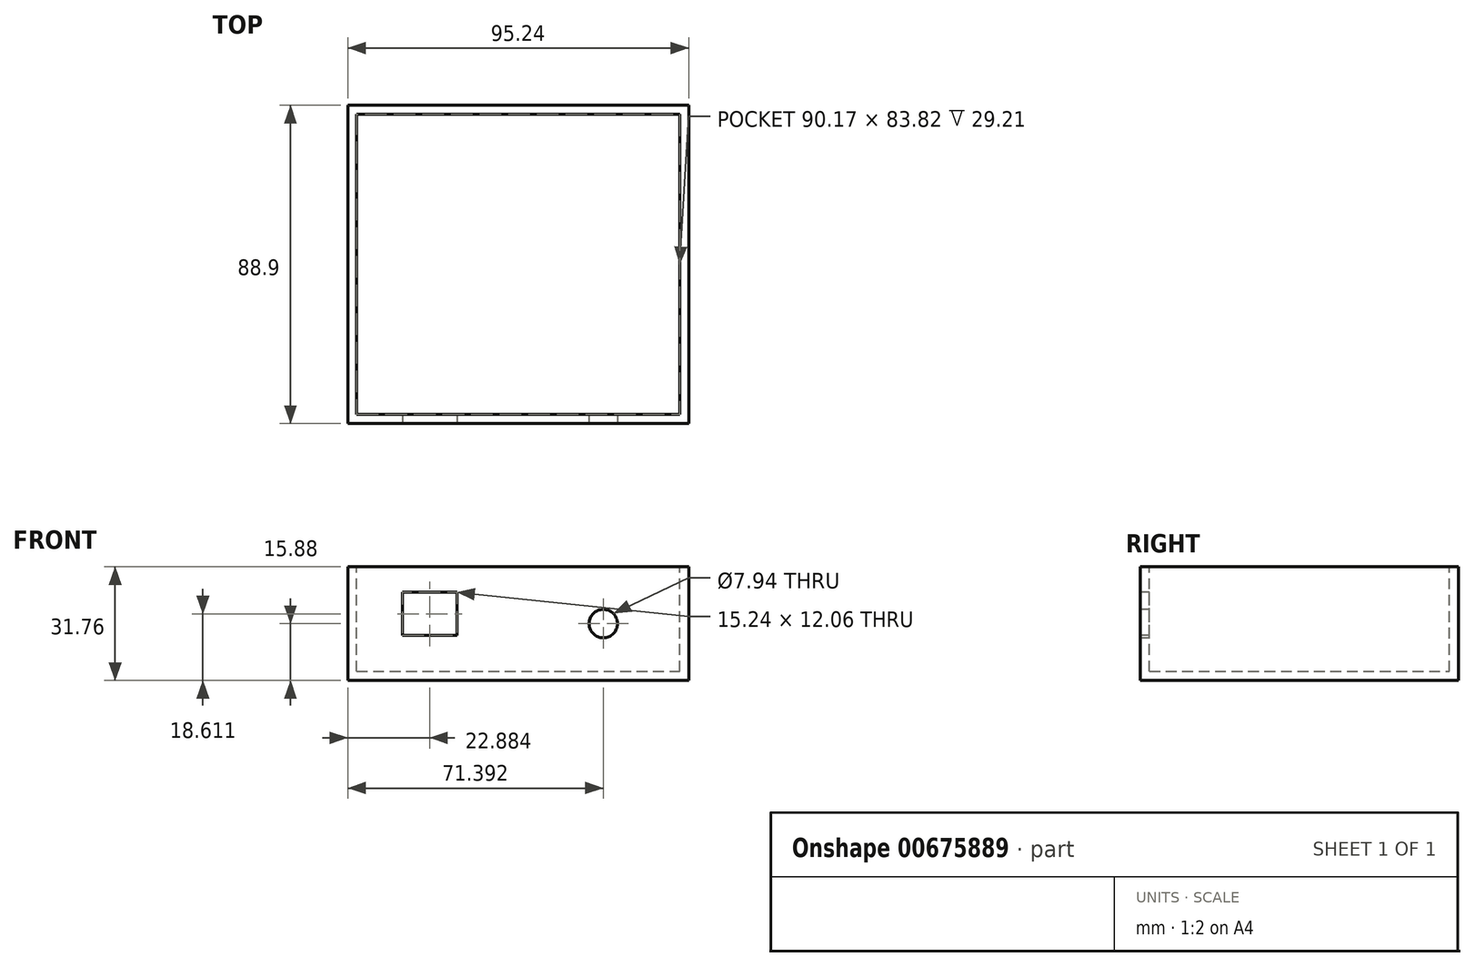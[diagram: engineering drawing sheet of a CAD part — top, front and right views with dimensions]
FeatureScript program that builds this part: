
annotation { "Feature Type Name" : "Feature", "Feature Type Description" : "" }
export const myFeature = defineFeature(function(context is Context, id is Id, definition is map)
    precondition{}
    {
        {
            var Q0;
            Q0=qCreatedBy(makeId("Front.planeOp"),FACE);
            var sketch = newSketch(context, id + "F0", { "sketchPlane" : qUnion([Q0])});
            skLineSegment(sketch, "E0.bottom", {"start": v(-47.62, -15.87) * mm, "end": v(47.63, -15.87) * mm});
            skLineSegment(sketch, "E0.top", {"start": v(-47.63, 15.87) * mm, "end": v(47.63, 15.87) * mm});
            skLineSegment(sketch, "E0.left", {"start": v(-47.63, -15.87) * mm, "end": v(-47.63, 15.87) * mm});
            skLineSegment(sketch, "E0.right", {"start": v(47.63, -15.87) * mm, "end": v(47.63, 15.87) * mm});
            skPoint(sketch, "E0.middle", {"position": v(0, 0) * mm});
            skSolve(sketch);
        }
        {
            var Q0;
            Q0 = qSketchRegion(id + "F0", true);
            extrude(context, id + "F1", {"entities" : qUnion([Q0]), "depth" : 88.9 * mm, "offsetDistance" : 25.4 * mm});
        }
        {
            var Q0;
            Q0=makeQuery(id+"F1.opExtrude","SWEPT_FACE",FACE,{"disambiguationData":[OSD([sQuery(id+"F0.wireOp",EDGE,"E0.top")])]});
            shell(context, id + "F2", {"entities" : qUnion([Q0]), "thickness" : 2.54 * mm});
        }
        {
            var Q0;
            Q0=makeQuery(id+"F1.opExtrude","CAP_FACE",FACE,{"disambiguationData":[OSD([sQuery(id+"F0.wireOp",EDGE,"E0.bottom"),sQuery(id+"F0.wireOp",EDGE,"E0.top"),sQuery(id+"F0.wireOp",EDGE,"E0.left"),sQuery(id+"F0.wireOp",EDGE,"E0.right")])],"isStart":false});
            var sketch = newSketch(context, id + "F3", { "sketchPlane" : qUnion([Q0])});
            skPoint(sketch, "E1", {"position": v(23.77, 0) * mm});
            skSolve(sketch);
        }
        {
            var Q0;
            Q0=sQuery(id+"F3.wireOp",VERTEX,"E1");
            var Q1;
            Q1=makeQuery(id+"F1.opExtrude","SWEPT_BODY",BODY,{"disambiguationData":[OSD([sQuery(id+"F0.wireOp",EDGE,"E0.bottom"),sQuery(id+"F0.wireOp",EDGE,"E0.top"),sQuery(id+"F0.wireOp",EDGE,"E0.left"),sQuery(id+"F0.wireOp",EDGE,"E0.right")])]});
            hole(context, id + "F4", {"style" : HoleStyle.SIMPLE, "endStyle" : HoleEndStyle.BLIND, "holeDiameter" : 7.94 * mm, "majorDiameter" : 6.35 * mm, "holeDepth" : 12.7 * mm, "isTappedThrough" : true, "tappedDepth" : 12.7 * mm, "tapClearance" : 3, "locations" : qUnion([Q0]), "scope" : qUnion([Q1])});
        }
        {
            var Q0;
            Q0=makeQuery(id+"F1.opExtrude","CAP_FACE",FACE,{"disambiguationData":[OSD([sQuery(id+"F0.wireOp",EDGE,"E0.bottom"),sQuery(id+"F0.wireOp",EDGE,"E0.top"),sQuery(id+"F0.wireOp",EDGE,"E0.left"),sQuery(id+"F0.wireOp",EDGE,"E0.right")])],"isStart":false});
            var sketch = newSketch(context, id + "F5", { "sketchPlane" : qUnion([Q0])});
            skLineSegment(sketch, "E2.bottom", {"start": v(-32.36, 8.76) * mm, "end": v(-17.12, 8.76) * mm});
            skLineSegment(sketch, "E2.top", {"start": v(-32.36, -3.3) * mm, "end": v(-17.12, -3.3) * mm});
            skLineSegment(sketch, "E2.left", {"start": v(-32.36, 8.76) * mm, "end": v(-32.36, -3.3) * mm});
            skLineSegment(sketch, "E2.right", {"start": v(-17.12, 8.76) * mm, "end": v(-17.12, -3.3) * mm});
            skSolve(sketch);
        }
        {
            var Q0;
            Q0=makeQuery(id+"F5.imprint","IMPRINT",FACE,{"disambiguationData":[TD([[makeQuery(id+"F5.imprint","IMPRINT",EDGE,{"derivedFrom":sQuery(id+"F5.wireOp",EDGE,"E2.bottom")}),-1.0]])]});
            extrude(context, id + "F6", {"entities" : qUnion([Q0]), "operationType" : NewBodyOperationType.REMOVE, "endBound" : BoundingType.UP_TO_NEXT, "oppositeDirection" : true, "depth" : 25.4 * mm, "offsetDistance" : 25.4 * mm});
        }
    });
